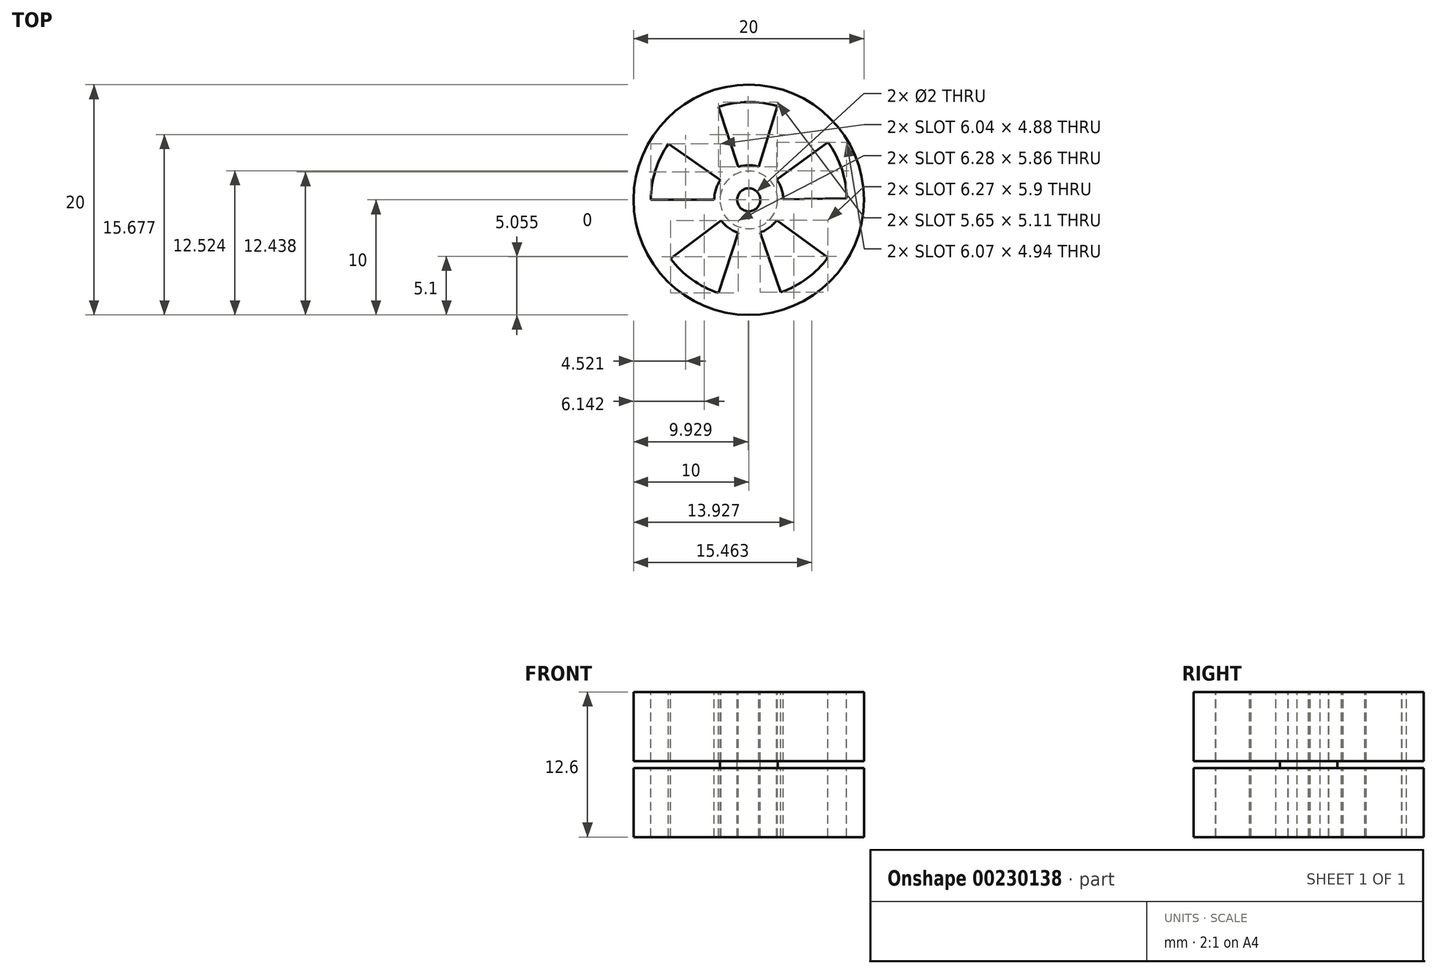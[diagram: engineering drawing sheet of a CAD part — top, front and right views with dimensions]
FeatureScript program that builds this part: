
annotation { "Feature Type Name" : "Feature", "Feature Type Description" : "" }
export const myFeature = defineFeature(function(context is Context, id is Id, definition is map)
    precondition{}
    {
        {
            var Q0;
            Q0=qCreatedBy(makeId("Top.planeOp"),FACE);
            var sketch = newSketch(context, id + "F0", { "sketchPlane" : qUnion([Q0])});
            skCircle(sketch, "E0", {"center": v(0, 0) * mm, "radius": 10 * mm});
            skSolve(sketch);
        }
        {
            var Q0;
            Q0=makeQuery(id+"F0.imprint","IMPRINT",FACE,{"disambiguationData":[TD([[makeQuery(id+"F0.imprint","IMPRINT",EDGE,{"derivedFrom":sQuery(id+"F0.wireOp",EDGE,"E0")}),1.0]])]});
            extrude(context, id + "F1", {"entities" : qUnion([Q0]), "depth" : 6 * mm});
        }
        {
            var Q0;
            Q0=makeQuery(id+"F1.opExtrude","CAP_FACE",FACE,{"disambiguationData":[OSD([sQuery(id+"F0.wireOp",EDGE,"E0")])],"isStart":false});
            var sketch = newSketch(context, id + "F2", { "sketchPlane" : qUnion([Q0])});
            skCircle(sketch, "E1", {"center": v(0, 0) * mm, "radius": 2.5 * mm});
            skSolve(sketch);
        }
        {
            var Q0;
            Q0=makeQuery(id+"F2.imprint","IMPRINT",FACE,{"disambiguationData":[TD([[makeQuery(id+"F2.imprint","IMPRINT",EDGE,{"derivedFrom":sQuery(id+"F2.wireOp",EDGE,"E1")}),1.0]])]});
            extrude(context, id + "F3", {"entities" : qUnion([Q0]), "operationType" : NewBodyOperationType.ADD, "depth" : 0.6 * mm});
        }
        {
            var Q0;
            Q0=makeQuery(id+"F3.opExtrude","CAP_FACE",FACE,{"disambiguationData":[OSD([sQuery(id+"F2.wireOp",EDGE,"E1")])],"isStart":false});
            var sketch = newSketch(context, id + "F4", { "sketchPlane" : qUnion([Q0])});
            skCircle(sketch, "E2", {"center": v(0, 0) * mm, "radius": 10 * mm});
            skSolve(sketch);
        }
        {
            var Q0;
            Q0 = qSketchRegion(id + "F4", true);
            extrude(context, id + "F5", {"entities" : qUnion([Q0]), "depth" : 6 * mm});
        }
        {
            var Q0;
            Q0=makeQuery(id+"F5.opExtrude","CAP_FACE",FACE,{"disambiguationData":[OSD([sQuery(id+"F4.wireOp",EDGE,"E2")])],"isStart":false});
            var sketch = newSketch(context, id + "F6", { "sketchPlane" : qUnion([Q0])});
            skCircle(sketch, "E3", {"center": v(0, 0) * mm, "radius": 1 * mm});
            skSolve(sketch);
        }
        {
            var Q0;
            Q0 = qSketchRegion(id + "F6", true);
            extrude(context, id + "F7", {"entities" : qUnion([Q0]), "operationType" : NewBodyOperationType.REMOVE, "oppositeDirection" : true, "depth" : 25 * mm});
        }
        {
            var Q0;
            Q0=makeQuery(id+"F5.opExtrude","CAP_FACE",FACE,{"disambiguationData":[OSD([sQuery(id+"F4.wireOp",EDGE,"E2")])],"isStart":false});
            var sketch = newSketch(context, id + "F8", { "sketchPlane" : qUnion([Q0])});
            skLineSegment(sketch, "E4", {"start": v(-3, 0) * mm, "end": v(-8.5, 0) * mm});
            skLineSegment(sketch, "E5", {"start": v(-6.96, 4.88) * mm, "end": v(-2.46, 1.72) * mm});
            skArc(sketch, "E6", {"start": v(-2.46, 1.72) * mm, "mid": v(-2.86, 0.9) * mm, "end": v(-3, 0) * mm});
            skArc(sketch, "E7", {"start": v(-8.5, 0) * mm, "mid": v(-8.1, 2.56) * mm, "end": v(-6.96, 4.88) * mm});
            skLineSegment(sketch, "E8.1.0", {"start": v(-6.79, -5.12) * mm, "end": v(-2.4, -1.8) * mm});
            skArc(sketch, "E8.1.1", {"start": v(-2.63, -8.08) * mm, "mid": v(-4.94, -6.92) * mm, "end": v(-6.79, -5.12) * mm});
            skLineSegment(sketch, "E8.1.2", {"start": v(-0.93, -2.85) * mm, "end": v(-2.63, -8.08) * mm});
            skArc(sketch, "E8.1.3", {"start": v(-2.4, -1.8) * mm, "mid": v(-1.74, -2.44) * mm, "end": v(-0.93, -2.85) * mm});
            skLineSegment(sketch, "E8.2.0", {"start": v(2.77, -8.04) * mm, "end": v(0.98, -2.84) * mm});
            skArc(sketch, "E8.2.1", {"start": v(6.88, -5) * mm, "mid": v(5.06, -6.83) * mm, "end": v(2.77, -8.04) * mm});
            skLineSegment(sketch, "E8.2.2", {"start": v(2.43, -1.76) * mm, "end": v(6.88, -5) * mm});
            skArc(sketch, "E8.2.3", {"start": v(0.98, -2.84) * mm, "mid": v(1.78, -2.41) * mm, "end": v(2.43, -1.76) * mm});
            skLineSegment(sketch, "E8.3.0", {"start": v(8.5, 0.15) * mm, "end": v(3, 0.05) * mm});
            skArc(sketch, "E8.3.1", {"start": v(6.88, 5) * mm, "mid": v(8.06, 2.7) * mm, "end": v(8.5, 0.15) * mm});
            skLineSegment(sketch, "E8.3.2", {"start": v(2.43, 1.76) * mm, "end": v(6.88, 5) * mm});
            skArc(sketch, "E8.3.3", {"start": v(3, 0.05) * mm, "mid": v(2.84, 0.95) * mm, "end": v(2.43, 1.76) * mm});
            skLineSegment(sketch, "E8.4.0", {"start": v(2.49, 8.13) * mm, "end": v(0.88, 2.87) * mm});
            skArc(sketch, "E8.4.1", {"start": v(-2.63, 8.08) * mm, "mid": v(-0.07, 8.5) * mm, "end": v(2.49, 8.13) * mm});
            skLineSegment(sketch, "E8.4.2", {"start": v(-0.93, 2.85) * mm, "end": v(-2.63, 8.08) * mm});
            skArc(sketch, "E8.4.3", {"start": v(0.88, 2.87) * mm, "mid": v(-0.03, 3) * mm, "end": v(-0.93, 2.85) * mm});
            skSolve(sketch);
        }
        {
            var Q0;
            Q0 = qSketchRegion(id + "F8", true);
            extrude(context, id + "F9", {"entities" : qUnion([Q0]), "operationType" : NewBodyOperationType.REMOVE, "endBound" : BoundingType.THROUGH_ALL, "oppositeDirection" : true, "depth" : 25 * mm});
        }
    });
